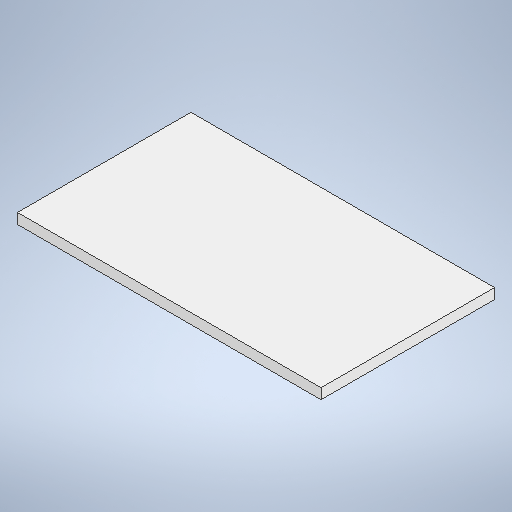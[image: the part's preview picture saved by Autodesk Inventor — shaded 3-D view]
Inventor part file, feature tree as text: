
AUTODESK INVENTOR PART (.ipt)
format: ipt  version: 2025 (Build 290162000, 162)  size: 245,248 bytes
history: native  units: in
note: dims shown in document units (in); Inventor stores cm internally (conversion verified against a paired STEP export)
features: extrude x1, sketch x1
ambient origin geometry x8: Origin, YZ Plane, XZ Plane, XY Plane, X Axis, Y Axis, Z Axis, Center Point
bodies: Solid1 (feature_tree)
feature tree (2):
  extrude  "Extrusion1"  Depth=43.75in
  sketch  "Sketch1"  dims[d6=25.0in d7=43.75in d8=1.5in d9=0.0in]
